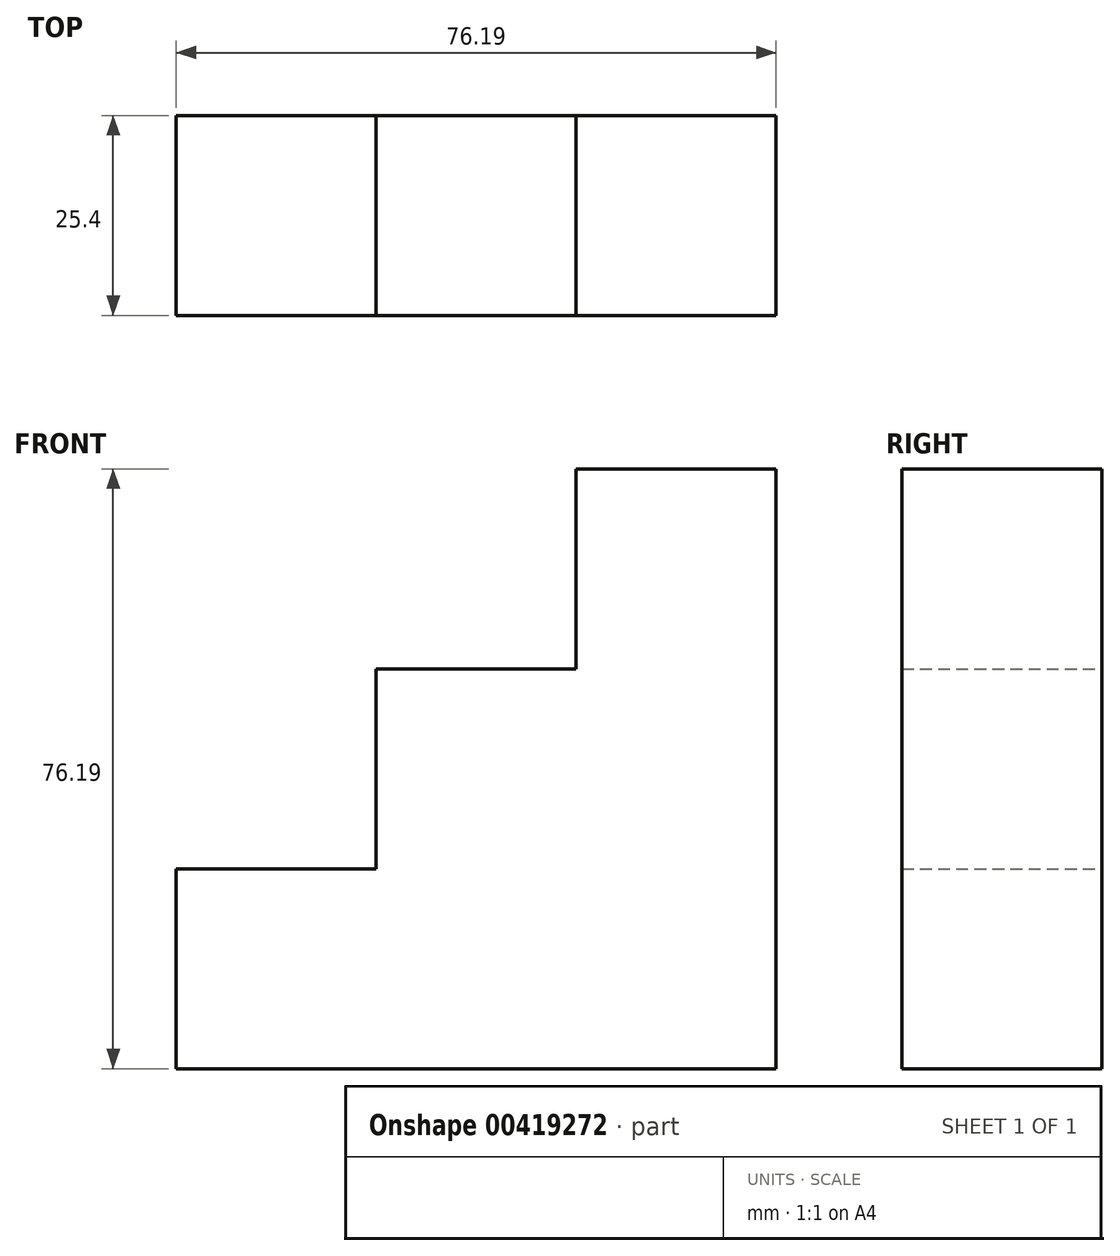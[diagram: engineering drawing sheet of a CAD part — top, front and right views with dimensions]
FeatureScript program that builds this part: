
annotation { "Feature Type Name" : "Feature", "Feature Type Description" : "" }
export const myFeature = defineFeature(function(context is Context, id is Id, definition is map)
    precondition{}
    {
        {
            var Q0;
            Q0=qCreatedBy(makeId("Front.planeOp"),FACE);
            var sketch = newSketch(context, id + "F0", { "sketchPlane" : qUnion([Q0])});
            skLineSegment(sketch, "E0", {"start": v(0, 0) * mm, "end": v(76.2, 0) * mm});
            skLineSegment(sketch, "E1", {"start": v(76.2, 0) * mm, "end": v(76.2, 76.2) * mm});
            skLineSegment(sketch, "E2", {"start": v(76.2, 76.2) * mm, "end": v(50.8, 76.2) * mm});
            skLineSegment(sketch, "E3", {"start": v(50.8, 76.2) * mm, "end": v(50.8, 50.8) * mm});
            skLineSegment(sketch, "E4", {"start": v(50.8, 50.8) * mm, "end": v(25.4, 50.8) * mm});
            skLineSegment(sketch, "E5", {"start": v(25.4, 50.8) * mm, "end": v(25.4, 25.4) * mm});
            skLineSegment(sketch, "E6", {"start": v(25.4, 25.4) * mm, "end": v(0, 25.4) * mm});
            skLineSegment(sketch, "E7", {"start": v(0, 25.4) * mm, "end": v(0, 0) * mm});
            skSolve(sketch);
        }
        {
            var Q0;
            Q0=makeQuery(id+"F0.imprint","IMPRINT",FACE,{"disambiguationData":[TD([[makeQuery(id+"F0.imprint","IMPRINT",EDGE,{"derivedFrom":sQuery(id+"F0.wireOp",EDGE,"E0")}),1.0]])]});
            extrude(context, id + "F1", {"entities" : qUnion([Q0]), "depth" : 25.4 * mm});
        }
    });
